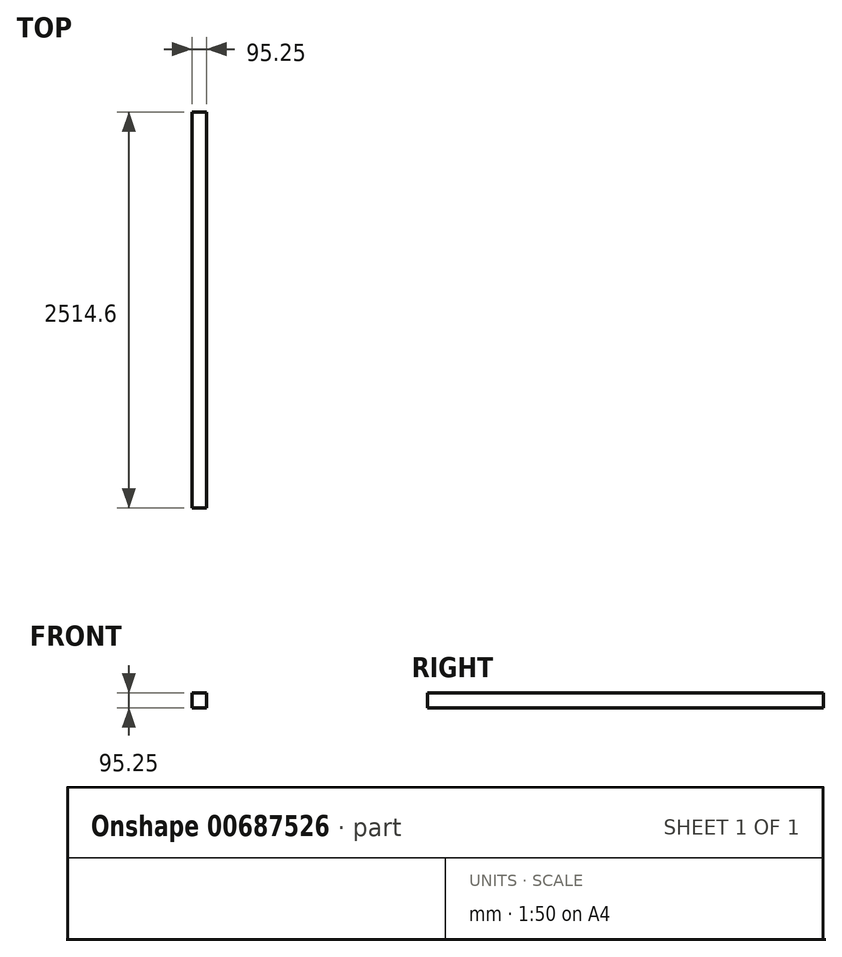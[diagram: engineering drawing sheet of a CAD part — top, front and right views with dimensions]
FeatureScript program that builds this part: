
annotation { "Feature Type Name" : "Feature", "Feature Type Description" : "" }
export const myFeature = defineFeature(function(context is Context, id is Id, definition is map)
    precondition{}
    {
        {
            var Q0;
            Q0=qCreatedBy(makeId("Front.planeOp"),FACE);
            var sketch = newSketch(context, id + "F0", { "sketchPlane" : qUnion([Q0])});
            skLineSegment(sketch, "E0.bottom", {"start": v(0, 0) * mm, "end": v(95.25, 0) * mm});
            skLineSegment(sketch, "E0.top", {"start": v(0, 95.25) * mm, "end": v(95.25, 95.25) * mm});
            skLineSegment(sketch, "E0.left", {"start": v(0, 0) * mm, "end": v(0, 95.25) * mm});
            skLineSegment(sketch, "E0.right", {"start": v(95.25, 0) * mm, "end": v(95.25, 95.25) * mm});
            skSolve(sketch);
        }
        {
            var Q0;
            Q0=makeQuery(id+"F0.imprint","IMPRINT",FACE,{"disambiguationData":[TD([[makeQuery(id+"F0.imprint","IMPRINT",EDGE,{"derivedFrom":sQuery(id+"F0.wireOp",EDGE,"E0.bottom")}),1.0]])]});
            extrude(context, id + "F1", {"entities" : qUnion([Q0]), "depth" : 2514.6 * mm, "offsetDistance" : 25.4 * mm});
        }
    });
